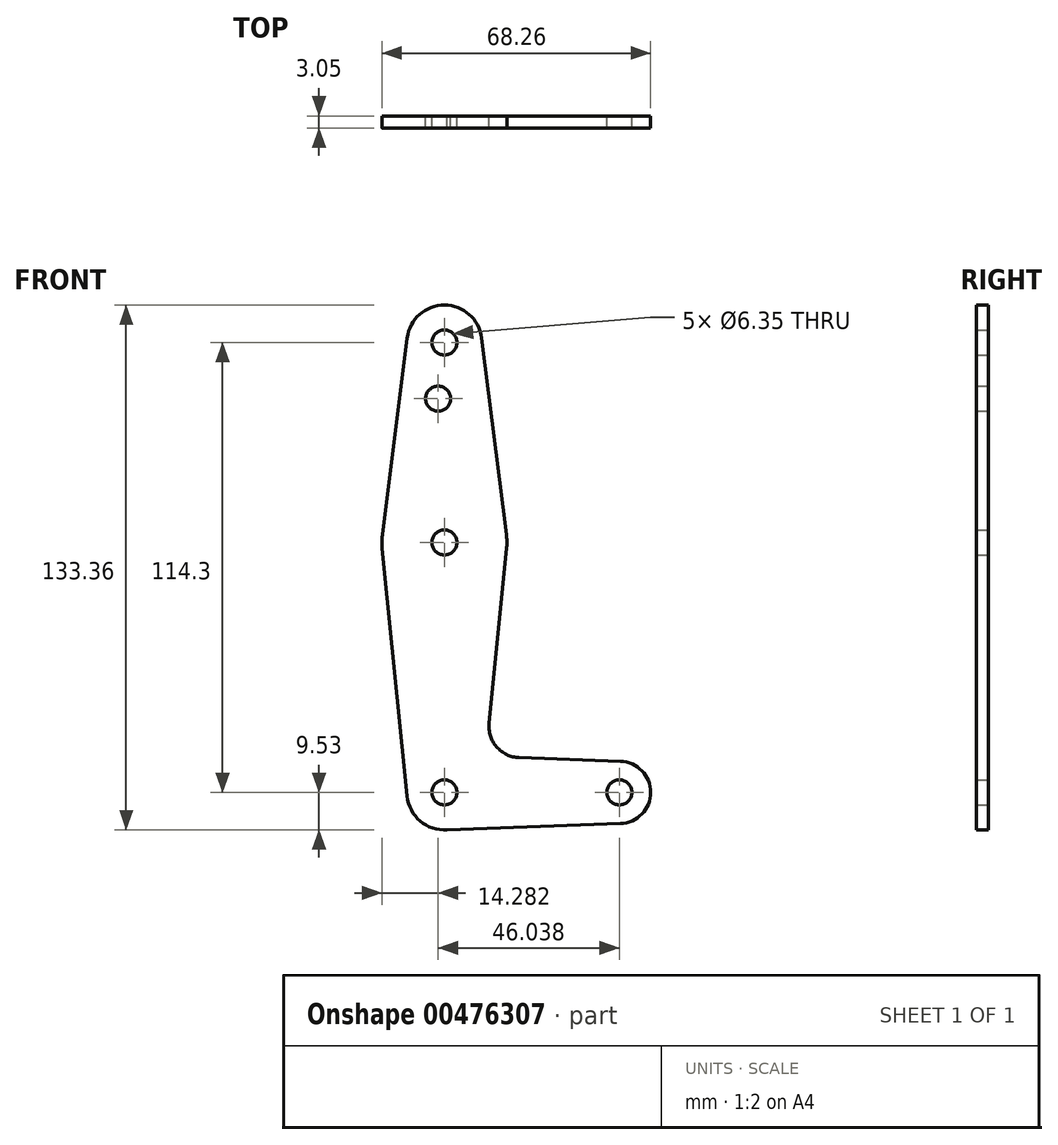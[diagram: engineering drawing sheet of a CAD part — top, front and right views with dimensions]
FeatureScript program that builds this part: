
annotation { "Feature Type Name" : "Feature", "Feature Type Description" : "" }
export const myFeature = defineFeature(function(context is Context, id is Id, definition is map)
    precondition{}
    {
        {
            var Q0;
            Q0=qCreatedBy(makeId("Front.planeOp"),FACE);
            var sketch = newSketch(context, id + "F0", { "sketchPlane" : qUnion([Q0])});
            skCircle(sketch, "E0", {"center": v(0, 0) * mm, "radius": 9.53 * mm});
            skCircle(sketch, "E1", {"center": v(44.45, 0) * mm, "radius": 7.94 * mm});
            skCircle(sketch, "E2", {"center": v(0, 63.5) * mm, "radius": 15.88 * mm});
            skCircle(sketch, "E3", {"center": v(0, 114.3) * mm, "radius": 9.53 * mm});
            skLineSegment(sketch, "E4", {"start": v(0, 0) * mm, "end": v(44.45, 0) * mm, "construction": true});
            skLineSegment(sketch, "E5", {"start": v(0, 0) * mm, "end": v(0, 114.3) * mm, "construction": true});
            skLineSegment(sketch, "E6", {"start": v(-9.45, 115.5) * mm, "end": v(-15.75, 65.48) * mm});
            skLineSegment(sketch, "E7", {"start": v(9.45, 115.5) * mm, "end": v(15.75, 65.48) * mm});
            skLineSegment(sketch, "E8", {"start": v(-15.8, 61.91) * mm, "end": v(-9.48, -0.95) * mm});
            skLineSegment(sketch, "E9", {"start": v(15.8, 61.91) * mm, "end": v(11.34, 17.59) * mm});
            skLineSegment(sketch, "E10", {"start": v(0, -9.53) * mm, "end": v(44.73, -7.93) * mm});
            skLineSegment(sketch, "E11", {"start": v(18.97, 8.85) * mm, "end": v(44.73, 7.93) * mm});
            skCircle(sketch, "E12", {"center": v(0, 114.3) * mm, "radius": 3.18 * mm});
            skCircle(sketch, "E13", {"center": v(0, 63.5) * mm, "radius": 3.18 * mm});
            skCircle(sketch, "E14", {"center": v(0, 0) * mm, "radius": 3.18 * mm});
            skCircle(sketch, "E15", {"center": v(44.45, 0) * mm, "radius": 3.18 * mm});
            skCircle(sketch, "E16", {"center": v(-1.59, 100.03) * mm, "radius": 3.18 * mm});
            skArc(sketch, "E17.filletArc", {"start": v(11.34, 17.59) * mm, "mid": v(13.26, 11.57) * mm, "end": v(18.97, 8.85) * mm});
            skSolve(sketch);
        }
        {
            var Q0;
            Q0 = qSketchRegion(id + "F0", true);
            extrude(context, id + "F1", {"entities" : qUnion([Q0]), "depth" : 3.05 * mm});
        }
    });
